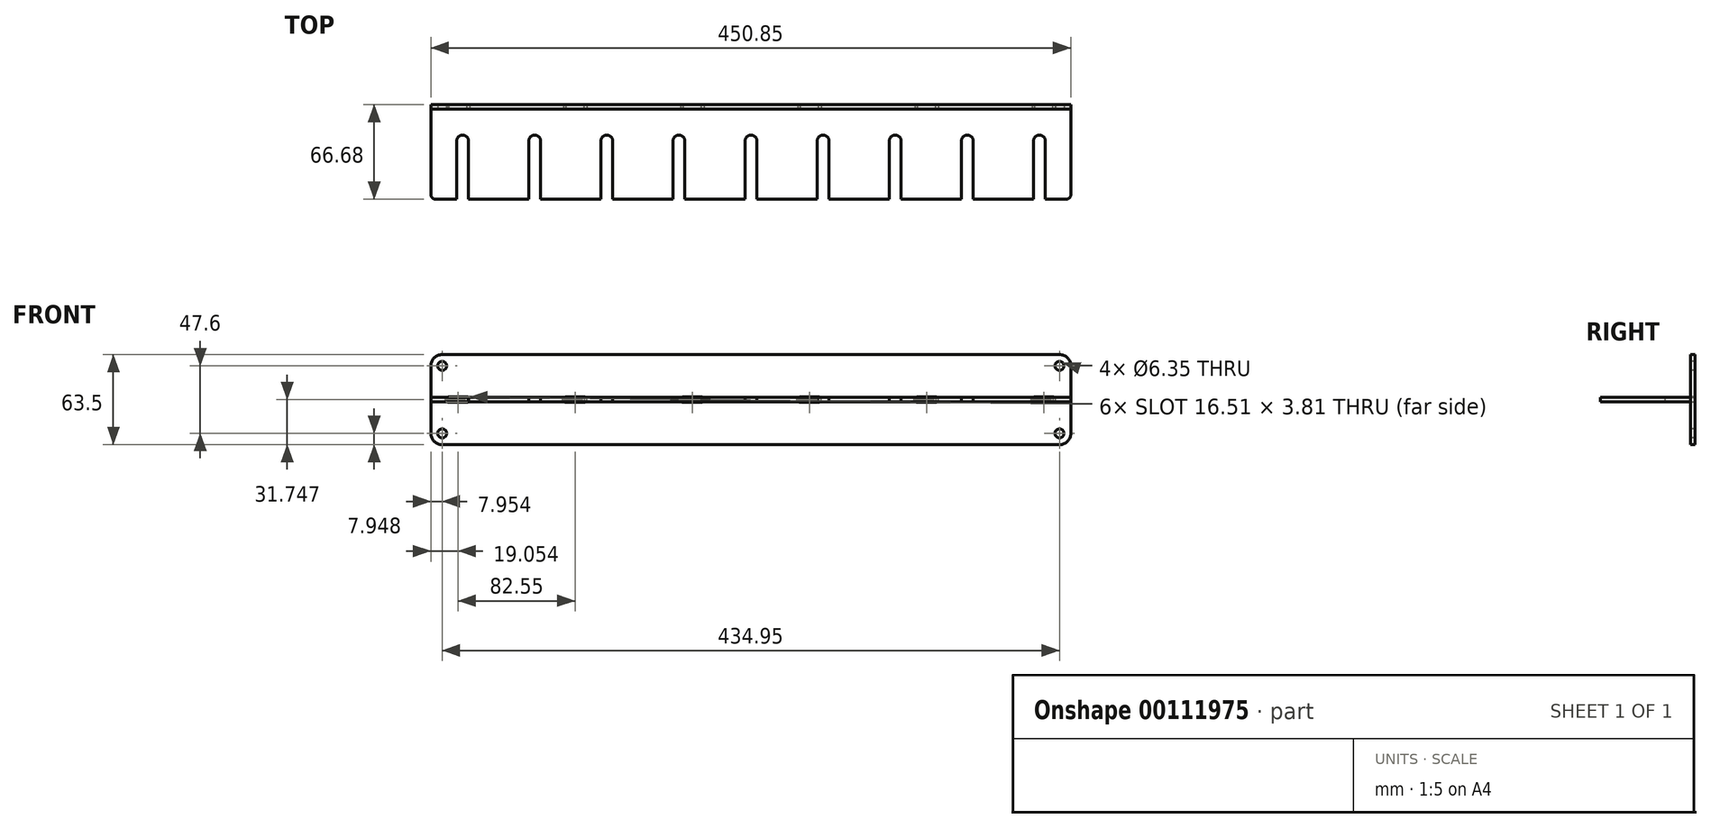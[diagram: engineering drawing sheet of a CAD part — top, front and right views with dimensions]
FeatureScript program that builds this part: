
annotation { "Feature Type Name" : "Feature", "Feature Type Description" : "" }
export const myFeature = defineFeature(function(context is Context, id is Id, definition is map)
    precondition{}
    {
        {
            var Q0;
            Q0=qCreatedBy(makeId("Top.planeOp"),FACE);
            var sketch = newSketch(context, id + "F0", { "sketchPlane" : qUnion([Q0])});
            skLineSegment(sketch, "E0.bottom", {"start": v(-229.48, 0) * mm, "end": v(-216.78, 0) * mm});
            skLineSegment(sketch, "E0.top", {"start": v(-226.3, -63.5) * mm, "end": v(-211.24, -63.5) * mm});
            skLineSegment(sketch, "E0.left", {"start": v(-229.48, 0) * mm, "end": v(-229.48, -60.33) * mm});
            skLineSegment(sketch, "E0.right", {"start": v(221.37, 0) * mm, "end": v(221.37, -60.33) * mm});
            skPoint(sketch, "E1.visualSharp", {"position": v(-229.48, 0) * mm});
            skPoint(sketch, "E2.visualSharp", {"position": v(-229.48, -63.5) * mm});
            skArc(sketch, "E2.filletArc", {"start": v(-229.48, -60.33) * mm, "mid": v(-228.55, -62.57) * mm, "end": v(-226.3, -63.5) * mm});
            skPoint(sketch, "E3.visualSharp", {"position": v(221.37, -63.5) * mm});
            skArc(sketch, "E3.filletArc", {"start": v(218.2, -63.5) * mm, "mid": v(220.44, -62.57) * mm, "end": v(221.37, -60.33) * mm});
            skPoint(sketch, "E4.visualSharp", {"position": v(221.37, 0) * mm});
            skLineSegment(sketch, "E5", {"start": v(-207.11, -63.5) * mm, "end": v(-207.11, -22.4) * mm, "construction": true});
            skArc(sketch, "E6.0.endCap", {"start": v(-211.24, -22.4) * mm, "mid": v(-207.11, -18.28) * mm, "end": v(-202.98, -22.4) * mm});
            skLineSegment(sketch, "E6.0.left", {"start": v(-211.24, -63.5) * mm, "end": v(-211.24, -22.4) * mm});
            skLineSegment(sketch, "E6.0.right", {"start": v(-202.98, -63.5) * mm, "end": v(-202.98, -22.4) * mm});
            skLineSegment(sketch, "E7.1.0.0", {"start": v(-152.18, -63.5) * mm, "end": v(-152.18, -22.4) * mm});
            skLineSegment(sketch, "E7.1.0.1", {"start": v(-160.44, -63.5) * mm, "end": v(-160.44, -22.4) * mm});
            skArc(sketch, "E7.1.0.2", {"start": v(-160.44, -22.4) * mm, "mid": v(-156.31, -18.28) * mm, "end": v(-152.18, -22.4) * mm});
            skLineSegment(sketch, "E7.2.0.0", {"start": v(-101.38, -63.5) * mm, "end": v(-101.38, -22.4) * mm});
            skLineSegment(sketch, "E7.2.0.1", {"start": v(-109.64, -63.5) * mm, "end": v(-109.64, -22.4) * mm});
            skArc(sketch, "E7.2.0.2", {"start": v(-109.64, -22.4) * mm, "mid": v(-105.51, -18.28) * mm, "end": v(-101.38, -22.4) * mm});
            skLineSegment(sketch, "E7.3.0.0", {"start": v(-50.58, -63.5) * mm, "end": v(-50.58, -22.4) * mm});
            skLineSegment(sketch, "E7.3.0.1", {"start": v(-58.84, -63.5) * mm, "end": v(-58.84, -22.4) * mm});
            skArc(sketch, "E7.3.0.2", {"start": v(-58.84, -22.4) * mm, "mid": v(-54.71, -18.28) * mm, "end": v(-50.58, -22.4) * mm});
            skLineSegment(sketch, "E7.4.0.0", {"start": v(0.22, -63.5) * mm, "end": v(0.22, -22.4) * mm});
            skLineSegment(sketch, "E7.4.0.1", {"start": v(-8.04, -63.5) * mm, "end": v(-8.04, -22.4) * mm});
            skArc(sketch, "E7.4.0.2", {"start": v(-8.04, -22.4) * mm, "mid": v(-3.91, -18.28) * mm, "end": v(0.22, -22.4) * mm});
            skLineSegment(sketch, "E7.5.0.0", {"start": v(51.02, -63.5) * mm, "end": v(51.02, -22.4) * mm});
            skLineSegment(sketch, "E7.5.0.1", {"start": v(42.76, -63.5) * mm, "end": v(42.76, -22.4) * mm});
            skArc(sketch, "E7.5.0.2", {"start": v(42.76, -22.4) * mm, "mid": v(46.89, -18.28) * mm, "end": v(51.02, -22.4) * mm});
            skLineSegment(sketch, "E7.6.0.0", {"start": v(101.82, -63.5) * mm, "end": v(101.82, -22.4) * mm});
            skLineSegment(sketch, "E7.6.0.1", {"start": v(93.56, -63.5) * mm, "end": v(93.56, -22.4) * mm});
            skArc(sketch, "E7.6.0.2", {"start": v(93.56, -22.4) * mm, "mid": v(97.69, -18.28) * mm, "end": v(101.82, -22.4) * mm});
            skLineSegment(sketch, "E7.direction1", {"start": v(-202.98, -63.5) * mm, "end": v(-160.44, -63.5) * mm, "construction": true});
            skLineSegment(sketch, "E8.0.7.0", {"start": v(152.62, -63.5) * mm, "end": v(152.62, -22.4) * mm});
            skLineSegment(sketch, "E8.3.7.0", {"start": v(144.36, -63.5) * mm, "end": v(144.36, -22.4) * mm});
            skArc(sketch, "E8.6.7.0", {"start": v(144.36, -22.4) * mm, "mid": v(148.49, -18.28) * mm, "end": v(152.62, -22.4) * mm});
            skLineSegment(sketch, "E9.0.8.0", {"start": v(203.42, -63.5) * mm, "end": v(203.42, -22.4) * mm});
            skLineSegment(sketch, "E9.3.8.0", {"start": v(195.16, -63.5) * mm, "end": v(195.16, -22.4) * mm});
            skArc(sketch, "E9.6.8.0", {"start": v(195.16, -22.4) * mm, "mid": v(199.29, -18.28) * mm, "end": v(203.42, -22.4) * mm});
            skLineSegment(sketch, "E10.trimOffspring", {"start": v(-202.98, -63.5) * mm, "end": v(-160.44, -63.5) * mm});
            skLineSegment(sketch, "E11.trimOffspring", {"start": v(-101.38, -63.5) * mm, "end": v(-58.84, -63.5) * mm});
            skLineSegment(sketch, "E12.trimOffspring", {"start": v(-50.58, -63.5) * mm, "end": v(-8.04, -63.5) * mm});
            skLineSegment(sketch, "E13.trimOffspring", {"start": v(0.22, -63.5) * mm, "end": v(42.76, -63.5) * mm});
            skLineSegment(sketch, "E14.trimOffspring", {"start": v(51.02, -63.5) * mm, "end": v(93.56, -63.5) * mm});
            skLineSegment(sketch, "E15.trimOffspring", {"start": v(101.82, -63.5) * mm, "end": v(144.36, -63.5) * mm});
            skLineSegment(sketch, "E16.trimOffspring", {"start": v(152.62, -63.5) * mm, "end": v(195.16, -63.5) * mm});
            skLineSegment(sketch, "E17.trimOffspring", {"start": v(203.42, -63.5) * mm, "end": v(218.2, -63.5) * mm});
            skLineSegment(sketch, "E18.trimOffspring", {"start": v(-152.18, -63.5) * mm, "end": v(-109.64, -63.5) * mm});
            skLineSegment(sketch, "E19.top", {"start": v(-204.08, 3.05) * mm, "end": v(-216.78, 3.05) * mm});
            skLineSegment(sketch, "E19.left", {"start": v(-204.08, 0) * mm, "end": v(-204.08, 3.05) * mm});
            skLineSegment(sketch, "E19.right", {"start": v(-216.78, 0) * mm, "end": v(-216.78, 3.05) * mm});
            skPoint(sketch, "E19.middle", {"position": v(-210.43, 0) * mm});
            skLineSegment(sketch, "E20.1.0.0", {"start": v(-121.53, 0) * mm, "end": v(-121.53, 3.05) * mm});
            skLineSegment(sketch, "E20.1.0.2", {"start": v(-134.23, 0) * mm, "end": v(-134.23, 3.05) * mm});
            skLineSegment(sketch, "E20.1.0.3", {"start": v(-121.53, 3.05) * mm, "end": v(-134.23, 3.05) * mm});
            skLineSegment(sketch, "E20.2.0.0", {"start": v(-38.98, 0) * mm, "end": v(-38.98, 3.05) * mm});
            skLineSegment(sketch, "E20.2.0.2", {"start": v(-51.68, 0) * mm, "end": v(-51.68, 3.05) * mm});
            skLineSegment(sketch, "E20.2.0.3", {"start": v(-38.98, 3.05) * mm, "end": v(-51.68, 3.05) * mm});
            skLineSegment(sketch, "E20.3.0.0", {"start": v(43.57, 0) * mm, "end": v(43.57, 3.05) * mm});
            skLineSegment(sketch, "E20.3.0.2", {"start": v(30.87, 0) * mm, "end": v(30.87, 3.05) * mm});
            skLineSegment(sketch, "E20.3.0.3", {"start": v(43.57, 3.05) * mm, "end": v(30.87, 3.05) * mm});
            skLineSegment(sketch, "E20.4.0.0", {"start": v(126.12, 0) * mm, "end": v(126.12, 3.05) * mm});
            skLineSegment(sketch, "E20.4.0.2", {"start": v(113.42, 0) * mm, "end": v(113.42, 3.05) * mm});
            skLineSegment(sketch, "E20.4.0.3", {"start": v(126.12, 3.05) * mm, "end": v(113.42, 3.05) * mm});
            skLineSegment(sketch, "E20.5.0.0", {"start": v(208.67, 0) * mm, "end": v(208.67, 3.05) * mm});
            skLineSegment(sketch, "E20.5.0.2", {"start": v(195.97, 0) * mm, "end": v(195.97, 3.05) * mm});
            skLineSegment(sketch, "E20.5.0.3", {"start": v(208.67, 3.05) * mm, "end": v(195.97, 3.05) * mm});
            skLineSegment(sketch, "E20.direction1", {"start": v(-204.08, -3.05) * mm, "end": v(-134.23, -3.05) * mm, "construction": true});
            skPoint(sketch, "E21.orphan", {"position": v(-216.78, -3.05) * mm});
            skLineSegment(sketch, "E22.trimOffspring", {"start": v(-204.08, 0) * mm, "end": v(-134.23, 0) * mm});
            skLineSegment(sketch, "E23.trimOffspring", {"start": v(-121.53, 0) * mm, "end": v(-51.68, 0) * mm});
            skLineSegment(sketch, "E24.trimOffspring", {"start": v(-38.98, 0) * mm, "end": v(30.87, 0) * mm});
            skPoint(sketch, "E25.orphan", {"position": v(-38.98, -3.05) * mm});
            skPoint(sketch, "E26.orphan", {"position": v(-51.68, -3.05) * mm});
            skPoint(sketch, "E27.orphan", {"position": v(43.57, -3.05) * mm});
            skPoint(sketch, "E28.orphan", {"position": v(30.87, -3.05) * mm});
            skLineSegment(sketch, "E29.trimOffspring", {"start": v(43.57, 0) * mm, "end": v(113.42, 0) * mm});
            skLineSegment(sketch, "E30.trimOffspring", {"start": v(208.67, 0) * mm, "end": v(221.37, 0) * mm});
            skPoint(sketch, "E31.orphan", {"position": v(208.67, -3.05) * mm});
            skPoint(sketch, "E32.orphan", {"position": v(195.97, -3.05) * mm});
            skPoint(sketch, "E33.orphan", {"position": v(113.42, -3.05) * mm});
            skLineSegment(sketch, "E34.trimOffspring", {"start": v(126.12, 0) * mm, "end": v(195.97, 0) * mm});
            skSolve(sketch);
        }
        {
            var Q0;
            Q0=makeQuery(id+"F0.imprint","IMPRINT",FACE,{"disambiguationData":[TD([[makeQuery(id+"F0.imprint","IMPRINT",EDGE,{"derivedFrom":sQuery(id+"F0.wireOp",EDGE,"E0.bottom")}),-1.0]])]});
            extrude(context, id + "F1", {"entities" : qUnion([Q0]), "depth" : 3.17 * mm});
        }
        {
            var Q0;
            Q0=makeQuery(id+"F1.opExtrude","SWEPT_FACE",FACE,{"disambiguationData":[OSD([sQuery(id+"F0.wireOp",EDGE,"E22.trimOffspring")])]});
            var sketch = newSketch(context, id + "F2", { "sketchPlane" : qUnion([Q0])});
            skLineSegment(sketch, "E35.0.0", {"start": v(204.08, 0) * mm, "end": v(216.78, 0) * mm, "construction": true});
            skLineSegment(sketch, "E35.0.1", {"start": v(216.78, 0) * mm, "end": v(216.78, 3.18) * mm, "construction": true});
            skLineSegment(sketch, "E35.0.2", {"start": v(216.78, 3.18) * mm, "end": v(204.08, 3.18) * mm, "construction": true});
            skLineSegment(sketch, "E35.0.3", {"start": v(204.08, 3.18) * mm, "end": v(204.08, 0) * mm, "construction": true});
            skLineSegment(sketch, "E35.1.0", {"start": v(121.53, 0) * mm, "end": v(134.23, 0) * mm, "construction": true});
            skLineSegment(sketch, "E35.1.1", {"start": v(134.23, 0) * mm, "end": v(134.23, 3.18) * mm, "construction": true});
            skLineSegment(sketch, "E35.1.2", {"start": v(134.23, 3.18) * mm, "end": v(121.53, 3.18) * mm, "construction": true});
            skLineSegment(sketch, "E35.1.3", {"start": v(121.53, 3.18) * mm, "end": v(121.53, 0) * mm, "construction": true});
            skLineSegment(sketch, "E35.2.0", {"start": v(38.98, 0) * mm, "end": v(51.68, 0) * mm, "construction": true});
            skLineSegment(sketch, "E35.2.1", {"start": v(51.68, 0) * mm, "end": v(51.68, 3.18) * mm, "construction": true});
            skLineSegment(sketch, "E35.2.2", {"start": v(51.68, 3.18) * mm, "end": v(38.98, 3.18) * mm, "construction": true});
            skLineSegment(sketch, "E35.2.3", {"start": v(38.98, 3.18) * mm, "end": v(38.98, 0) * mm, "construction": true});
            skLineSegment(sketch, "E35.3.0", {"start": v(-43.57, 0) * mm, "end": v(-30.87, 0) * mm, "construction": true});
            skLineSegment(sketch, "E35.3.1", {"start": v(-30.87, 0) * mm, "end": v(-30.87, 3.18) * mm, "construction": true});
            skLineSegment(sketch, "E35.3.2", {"start": v(-30.87, 3.18) * mm, "end": v(-43.57, 3.18) * mm, "construction": true});
            skLineSegment(sketch, "E35.3.3", {"start": v(-43.57, 3.18) * mm, "end": v(-43.57, 0) * mm, "construction": true});
            skLineSegment(sketch, "E35.4.0", {"start": v(-126.12, 0) * mm, "end": v(-113.42, 0) * mm, "construction": true});
            skLineSegment(sketch, "E35.4.1", {"start": v(-113.42, 0) * mm, "end": v(-113.42, 3.18) * mm, "construction": true});
            skLineSegment(sketch, "E35.4.2", {"start": v(-113.42, 3.18) * mm, "end": v(-126.12, 3.18) * mm, "construction": true});
            skLineSegment(sketch, "E35.4.3", {"start": v(-126.12, 3.18) * mm, "end": v(-126.12, 0) * mm, "construction": true});
            skLineSegment(sketch, "E35.5.0", {"start": v(-208.67, 0) * mm, "end": v(-195.97, 0) * mm, "construction": true});
            skLineSegment(sketch, "E35.5.1", {"start": v(-195.97, 0) * mm, "end": v(-195.97, 3.18) * mm, "construction": true});
            skLineSegment(sketch, "E35.5.2", {"start": v(-195.97, 3.18) * mm, "end": v(-208.67, 3.18) * mm, "construction": true});
            skLineSegment(sketch, "E35.5.3", {"start": v(-208.67, 3.18) * mm, "end": v(-208.67, 0) * mm, "construction": true});
            skPoint(sketch, "E36.0", {"position": v(-221.37, 3.18) * mm});
            skLineSegment(sketch, "E37.bottom", {"start": v(-213.42, -30.16) * mm, "end": v(221.53, -30.16) * mm});
            skLineSegment(sketch, "E37.top", {"start": v(-213.42, 33.34) * mm, "end": v(221.53, 33.34) * mm});
            skLineSegment(sketch, "E37.left", {"start": v(-221.37, -22.21) * mm, "end": v(-221.37, 25.39) * mm});
            skLineSegment(sketch, "E37.right", {"start": v(229.48, -22.21) * mm, "end": v(229.48, 25.39) * mm});
            skPoint(sketch, "E38", {"position": v(-221.37, 1.59) * mm});
            skPoint(sketch, "E39", {"position": v(-208.67, 1.59) * mm});
            skPoint(sketch, "E40.visualSharp", {"position": v(229.48, 33.34) * mm});
            skArc(sketch, "E40.filletArc", {"start": v(229.48, 25.39) * mm, "mid": v(227.15, 31) * mm, "end": v(221.53, 33.34) * mm});
            skPoint(sketch, "E41.visualSharp", {"position": v(229.48, -30.16) * mm});
            skArc(sketch, "E41.filletArc", {"start": v(221.53, -30.16) * mm, "mid": v(227.15, -27.83) * mm, "end": v(229.48, -22.21) * mm});
            skPoint(sketch, "E42.visualSharp", {"position": v(-221.37, -30.16) * mm});
            skArc(sketch, "E42.filletArc", {"start": v(-221.37, -22.21) * mm, "mid": v(-219.05, -27.83) * mm, "end": v(-213.42, -30.16) * mm});
            skPoint(sketch, "E43.visualSharp", {"position": v(-221.37, 33.34) * mm});
            skArc(sketch, "E43.filletArc", {"start": v(-213.42, 33.34) * mm, "mid": v(-219.05, 31) * mm, "end": v(-221.37, 25.39) * mm});
            skLineSegment(sketch, "E44", {"start": v(216.78, 1.59) * mm, "end": v(204.08, 1.59) * mm});
            skLineSegment(sketch, "E45", {"start": v(134.23, 1.59) * mm, "end": v(121.53, 1.59) * mm});
            skLineSegment(sketch, "E46", {"start": v(51.68, 1.59) * mm, "end": v(38.98, 1.59) * mm});
            skLineSegment(sketch, "E47", {"start": v(-30.87, 1.59) * mm, "end": v(-43.57, 1.59) * mm});
            skLineSegment(sketch, "E48", {"start": v(-113.42, 1.59) * mm, "end": v(-126.12, 1.59) * mm});
            skLineSegment(sketch, "E49", {"start": v(-195.97, 1.59) * mm, "end": v(-208.67, 1.59) * mm});
            skArc(sketch, "E50.0.startCap", {"start": v(-195.97, 3.5) * mm, "mid": v(-194.07, 1.59) * mm, "end": v(-195.97, -0.32) * mm});
            skArc(sketch, "E50.0.endCap", {"start": v(-208.67, -0.32) * mm, "mid": v(-210.58, 1.59) * mm, "end": v(-208.67, 3.5) * mm});
            skLineSegment(sketch, "E50.0.left", {"start": v(-195.97, -0.32) * mm, "end": v(-208.67, -0.32) * mm});
            skLineSegment(sketch, "E50.0.right", {"start": v(-195.97, 3.5) * mm, "end": v(-208.67, 3.5) * mm});
            skArc(sketch, "E50.1.startCap", {"start": v(-113.42, 3.5) * mm, "mid": v(-111.52, 1.59) * mm, "end": v(-113.42, -0.32) * mm});
            skArc(sketch, "E50.1.endCap", {"start": v(-126.12, -0.32) * mm, "mid": v(-128.03, 1.59) * mm, "end": v(-126.12, 3.5) * mm});
            skLineSegment(sketch, "E50.1.left", {"start": v(-113.42, -0.32) * mm, "end": v(-126.12, -0.32) * mm});
            skLineSegment(sketch, "E50.1.right", {"start": v(-113.42, 3.5) * mm, "end": v(-126.12, 3.5) * mm});
            skArc(sketch, "E50.2.startCap", {"start": v(-30.87, 3.5) * mm, "mid": v(-28.97, 1.59) * mm, "end": v(-30.87, -0.32) * mm});
            skArc(sketch, "E50.2.endCap", {"start": v(-43.57, -0.32) * mm, "mid": v(-45.48, 1.59) * mm, "end": v(-43.57, 3.5) * mm});
            skLineSegment(sketch, "E50.2.left", {"start": v(-30.87, -0.32) * mm, "end": v(-43.57, -0.32) * mm});
            skLineSegment(sketch, "E50.2.right", {"start": v(-30.87, 3.5) * mm, "end": v(-43.57, 3.5) * mm});
            skArc(sketch, "E50.3.startCap", {"start": v(51.68, 3.5) * mm, "mid": v(53.58, 1.59) * mm, "end": v(51.68, -0.32) * mm});
            skArc(sketch, "E50.3.endCap", {"start": v(38.98, -0.32) * mm, "mid": v(37.07, 1.59) * mm, "end": v(38.98, 3.5) * mm});
            skLineSegment(sketch, "E50.3.left", {"start": v(51.68, -0.32) * mm, "end": v(38.98, -0.32) * mm});
            skLineSegment(sketch, "E50.3.right", {"start": v(51.68, 3.5) * mm, "end": v(38.98, 3.5) * mm});
            skArc(sketch, "E50.4.startCap", {"start": v(134.23, 3.5) * mm, "mid": v(136.13, 1.59) * mm, "end": v(134.23, -0.32) * mm});
            skArc(sketch, "E50.4.endCap", {"start": v(121.53, -0.32) * mm, "mid": v(119.62, 1.59) * mm, "end": v(121.53, 3.5) * mm});
            skLineSegment(sketch, "E50.4.left", {"start": v(134.23, -0.32) * mm, "end": v(121.53, -0.32) * mm});
            skLineSegment(sketch, "E50.4.right", {"start": v(134.23, 3.5) * mm, "end": v(121.53, 3.5) * mm});
            skArc(sketch, "E50.5.startCap", {"start": v(216.78, 3.5) * mm, "mid": v(218.68, 1.59) * mm, "end": v(216.78, -0.32) * mm});
            skArc(sketch, "E50.5.endCap", {"start": v(204.08, -0.32) * mm, "mid": v(202.17, 1.59) * mm, "end": v(204.08, 3.5) * mm});
            skLineSegment(sketch, "E50.5.left", {"start": v(216.78, -0.32) * mm, "end": v(204.08, -0.32) * mm});
            skLineSegment(sketch, "E50.5.right", {"start": v(216.78, 3.5) * mm, "end": v(204.08, 3.5) * mm});
            skCircle(sketch, "E51", {"center": v(221.53, 25.39) * mm, "radius": 3.18 * mm});
            skCircle(sketch, "E52", {"center": v(221.53, -22.21) * mm, "radius": 3.18 * mm});
            skCircle(sketch, "E53", {"center": v(-213.42, 25.39) * mm, "radius": 3.18 * mm});
            skCircle(sketch, "E54", {"center": v(-213.42, -22.21) * mm, "radius": 3.18 * mm});
            skSolve(sketch);
        }
        {
            var Q0;
            Q0 = qSketchRegion(id + "F2", true);
            extrude(context, id + "F3", {"entities" : qUnion([Q0]), "depth" : 3.17 * mm});
        }
    });
